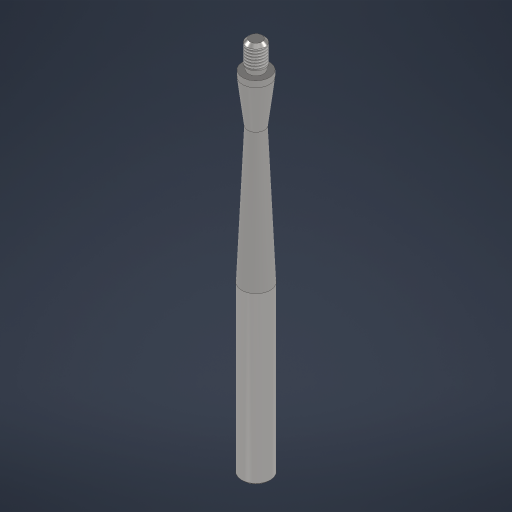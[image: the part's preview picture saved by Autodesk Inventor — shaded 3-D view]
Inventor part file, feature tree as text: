
AUTODESK INVENTOR PART (.ipt)
format: ipt  version: 2024.3 (Build 283343000, 343)  size: 233,472 bytes
history: native  units: mm
features: chamfer x3, sketch x2, revolve x1, thread x1, hole x1, other x1
ambient origin geometry x8: Origin, YZ Plane, XZ Plane, XY Plane, X Axis, Y Axis, Z Axis, Center Point
bodies: Solid1 (feature_tree)
feature tree (9):
  revolve  "Revolution1"  [1 undecoded]
  thread  "Thread1"  [1 undecoded]
  hole  "Hole1"  [1 undecoded]
  chamfer  "Chamfer2"  Distance=3.0mm
  chamfer  "Chamfer3"  Distance=18.0mm
  chamfer  "Chamfer4"  Distance=4.0mm
  sketch  "Sketch1"  dims[d0=250.0mm d1=19.0mm d2=110.0mm]
  sketch  "Sketch2"  dims[d5=11.14103mm d6=12.0mm d7=3.0mm d9=18.0mm d10=4.0mm d11=10.0mm d12=60.0deg d13=18.0mm d14=0.436332mm d15=90.0deg d16=1.218746mm d17=200.0mm d18=232.0mm d19=50.0mm d20=14.42265mm d21=13.268mm d22=0.0mm d23=15.0mm d24=0.5mm d25=15.5mm d26=2.0mm d27=90.0deg d28=80.0mm d29=20.594885mm d41=2.0mm d42=2.0mm d43=45.0deg d44=0.5mm d45=2.0mm d46=45.0deg d47=1.0mm d48=2.0mm d49=45.0deg]
  other  "Finish1"
note: 3 required parameter values undecoded (feature->parameter linkage not recoverable at this tier; creation-order binding heuristic only, values carry confidence <= 0.55)